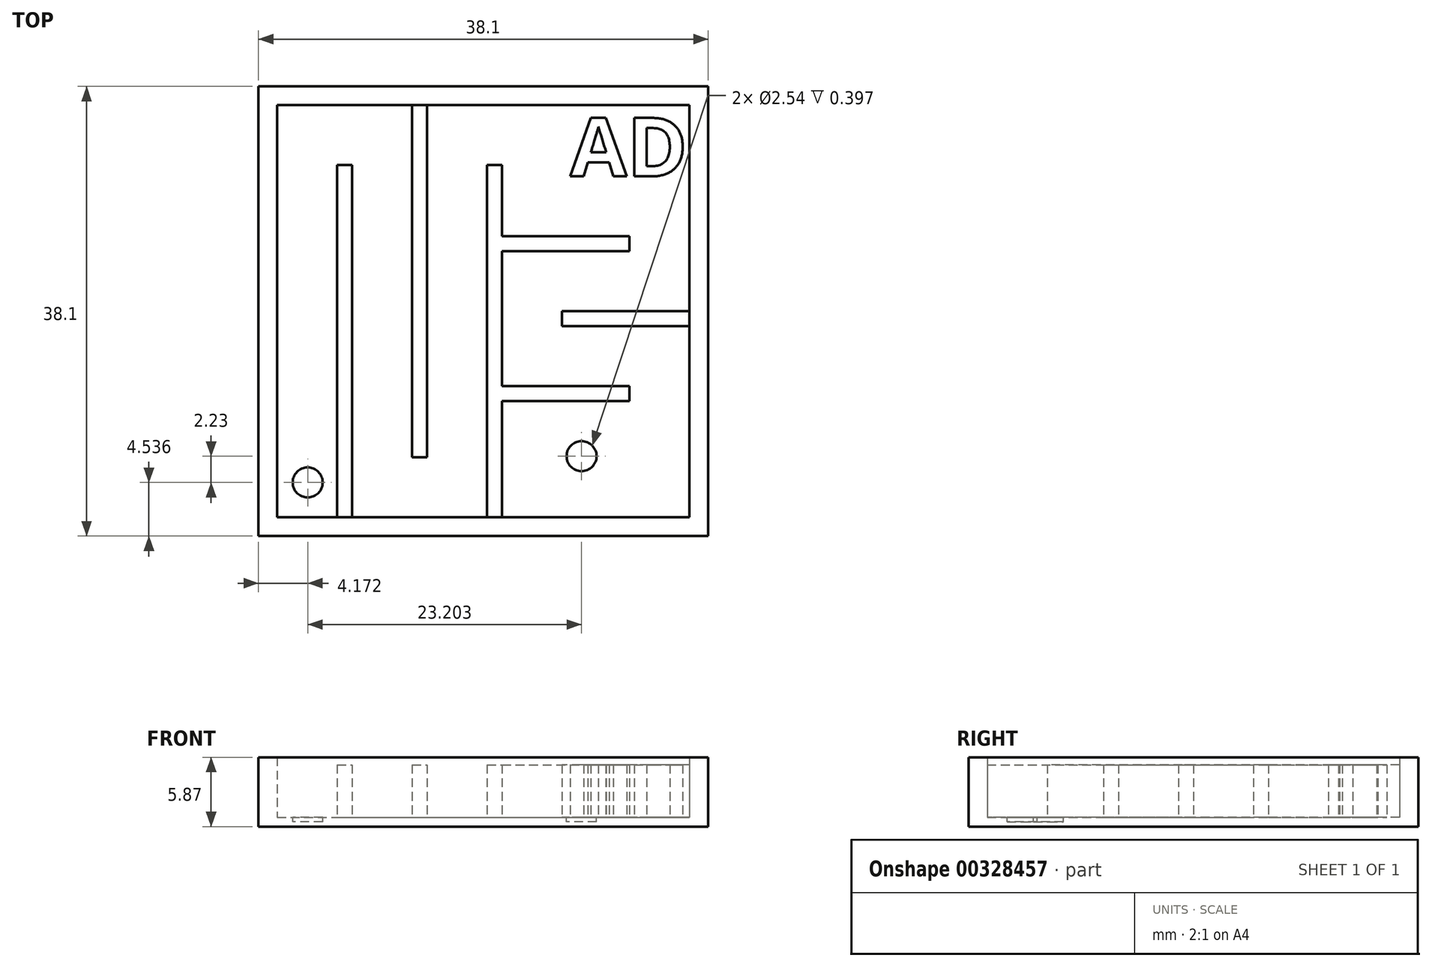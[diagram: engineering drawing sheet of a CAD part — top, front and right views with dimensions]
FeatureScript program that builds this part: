
annotation { "Feature Type Name" : "Feature", "Feature Type Description" : "" }
export const myFeature = defineFeature(function(context is Context, id is Id, definition is map)
    precondition{}
    {
        {
            var Q0;
            Q0=qCreatedBy(makeId("Top.planeOp"),FACE);
            var sketch = newSketch(context, id + "F0", { "sketchPlane" : qUnion([Q0])});
            skLineSegment(sketch, "E0.bottom", {"start": v(-18.05, 18.93) * mm, "end": v(20.05, 18.93) * mm});
            skLineSegment(sketch, "E0.top", {"start": v(-18.05, -19.17) * mm, "end": v(20.05, -19.17) * mm});
            skLineSegment(sketch, "E0.left", {"start": v(-18.05, 18.93) * mm, "end": v(-18.05, -19.17) * mm});
            skLineSegment(sketch, "E0.right", {"start": v(20.05, 18.93) * mm, "end": v(20.05, -19.17) * mm});
            skSolve(sketch);
        }
        {
            var Q0;
            Q0=makeQuery(id+"F0.imprint","IMPRINT",FACE,{"disambiguationData":[TD([[makeQuery(id+"F0.imprint","IMPRINT",EDGE,{"derivedFrom":sQuery(id+"F0.wireOp",EDGE,"E0.bottom")}),-1.0]])]});
            extrude(context, id + "F1", {"entities" : qUnion([Q0]), "depth" : 0.8 * mm});
        }
        {
            var Q0;
            Q0=makeQuery(id+"F1.opExtrude","CAP_FACE",FACE,{"disambiguationData":[OSD([sQuery(id+"F0.wireOp",EDGE,"E0.bottom"),sQuery(id+"F0.wireOp",EDGE,"E0.top"),sQuery(id+"F0.wireOp",EDGE,"E0.left"),sQuery(id+"F0.wireOp",EDGE,"E0.right")])],"isStart":false});
            var sketch = newSketch(context, id + "F2", { "sketchPlane" : qUnion([Q0])});
            skLineSegment(sketch, "E1.0", {"start": v(-16.46, 17.34) * mm, "end": v(18.46, 17.34) * mm});
            skLineSegment(sketch, "E1.1", {"start": v(-16.46, 17.34) * mm, "end": v(-16.46, -17.59) * mm});
            skLineSegment(sketch, "E1.2", {"start": v(-16.46, -17.59) * mm, "end": v(18.46, -17.59) * mm});
            skLineSegment(sketch, "E1.3", {"start": v(18.46, 17.34) * mm, "end": v(18.46, -17.59) * mm});
            skSolve(sketch);
        }
        {
            var Q0;
            Q0=makeQuery(id+"F2.imprint","IMPRINT",FACE,{"disambiguationData":[TD([[makeQuery(id+"F2.imprint","IMPRINT",EDGE,{"derivedFrom":sQuery(id+"F2.wireOp",EDGE,"E1.0")}),1.0]])]});
            extrude(context, id + "F3", {"entities" : qUnion([Q0]), "operationType" : NewBodyOperationType.ADD, "depth" : 5.08 * mm});
        }
        {
            var Q0;
            Q0=makeQuery(id+"F1.opExtrude","CAP_FACE",FACE,{"disambiguationData":[OSD([sQuery(id+"F0.wireOp",EDGE,"E0.bottom"),sQuery(id+"F0.wireOp",EDGE,"E0.top"),sQuery(id+"F0.wireOp",EDGE,"E0.left"),sQuery(id+"F0.wireOp",EDGE,"E0.right")])],"isStart":false});
            var sketch = newSketch(context, id + "F4", { "sketchPlane" : qUnion([Q0])});
            skLineSegment(sketch, "E2.bottom", {"start": v(-11.38, -17.59) * mm, "end": v(-10.11, -17.59) * mm});
            skLineSegment(sketch, "E2.top", {"start": v(-11.38, 12.26) * mm, "end": v(-10.11, 12.26) * mm});
            skLineSegment(sketch, "E2.left", {"start": v(-11.38, -17.59) * mm, "end": v(-11.38, 12.26) * mm});
            skLineSegment(sketch, "E2.right", {"start": v(-10.11, -17.59) * mm, "end": v(-10.11, 12.26) * mm});
            skLineSegment(sketch, "E3.bottom", {"start": v(-5.03, 17.34) * mm, "end": v(-3.76, 17.34) * mm});
            skLineSegment(sketch, "E3.top", {"start": v(-5.03, -12.5) * mm, "end": v(-3.76, -12.5) * mm});
            skLineSegment(sketch, "E3.left", {"start": v(-5.03, 17.34) * mm, "end": v(-5.03, -12.5) * mm});
            skLineSegment(sketch, "E3.right", {"start": v(-3.76, 17.34) * mm, "end": v(-3.76, -12.5) * mm});
            skLineSegment(sketch, "E4.bottom", {"start": v(1.32, -17.59) * mm, "end": v(2.59, -17.59) * mm});
            skLineSegment(sketch, "E4.top", {"start": v(1.32, 12.26) * mm, "end": v(2.59, 12.26) * mm});
            skLineSegment(sketch, "E4.left", {"start": v(1.32, -17.59) * mm, "end": v(1.32, 12.26) * mm});
            skLineSegment(sketch, "E4.right", {"start": v(2.59, -17.59) * mm, "end": v(2.59, 12.26) * mm});
            skLineSegment(sketch, "E5.bottom", {"start": v(2.59, 6.23) * mm, "end": v(13.38, 6.23) * mm});
            skLineSegment(sketch, "E5.top", {"start": v(2.59, 4.96) * mm, "end": v(13.38, 4.96) * mm});
            skLineSegment(sketch, "E5.left", {"start": v(2.59, 6.23) * mm, "end": v(2.59, 4.96) * mm});
            skLineSegment(sketch, "E5.right", {"start": v(13.38, 6.23) * mm, "end": v(13.38, 4.96) * mm});
            skLineSegment(sketch, "E6.bottom", {"start": v(18.46, -0.12) * mm, "end": v(7.67, -0.12) * mm});
            skLineSegment(sketch, "E6.top", {"start": v(18.46, -1.4) * mm, "end": v(7.67, -1.4) * mm});
            skLineSegment(sketch, "E6.left", {"start": v(18.46, -0.12) * mm, "end": v(18.46, -1.4) * mm});
            skLineSegment(sketch, "E6.right", {"start": v(7.67, -0.12) * mm, "end": v(7.67, -1.4) * mm});
            skLineSegment(sketch, "E7.bottom", {"start": v(2.59, -7.74) * mm, "end": v(13.38, -7.74) * mm});
            skLineSegment(sketch, "E7.top", {"start": v(2.59, -6.47) * mm, "end": v(13.38, -6.47) * mm});
            skLineSegment(sketch, "E7.left", {"start": v(2.59, -7.74) * mm, "end": v(2.59, -6.47) * mm});
            skLineSegment(sketch, "E7.right", {"start": v(13.38, -7.74) * mm, "end": v(13.38, -6.47) * mm});
            skCircle(sketch, "E8", {"center": v(9.32, -12.4) * mm, "radius": 1.27 * mm});
            skText(sketch, "E9", { "text": "AD", "fontName": "OpenSans-Bold.ttf"});
            skCircle(sketch, "E10", {"center": v(-13.88, -14.63) * mm, "radius": 1.27 * mm});
            const initialGuessF4  = {"E9": [0.00836, 0.0113, 1, 0, 0.005]};
            skSetInitialGuess(sketch, initialGuessF4);
            skSolve(sketch);
        }
        {
            var Q0;
            Q0=makeQuery(id+"F4.imprint","IMPRINT",FACE,{"disambiguationData":[TD([[makeQuery(id+"F4.imprint","IMPRINT",EDGE,{"derivedFrom":sQuery(id+"F4.wireOp",EDGE,"E2.bottom")}),1.0]])]});
            var Q1;
            Q1=makeQuery(id+"F4.imprint","IMPRINT",FACE,{"disambiguationData":[TD([[makeQuery(id+"F4.imprint","IMPRINT",EDGE,{"derivedFrom":sQuery(id+"F4.wireOp",EDGE,"E3.bottom")}),-1.0]])]});
            var Q2;
            {var subQ1=sQuery(id+"F4.wireOp",EDGE,"E4.bottom");Q2=makeQuery(id+"F4.imprint","IMPRINT",FACE,{"disambiguationData":[TD([[makeQuery(id+"F4.imprint","IMPRINT",EDGE,{"derivedFrom":subQ1}),1.0]])]});}
            var Q3;
            Q3=makeQuery(id+"F4.imprint","IMPRINT",FACE,{"disambiguationData":[TD([[makeQuery(id+"F4.imprint","IMPRINT",EDGE,{"derivedFrom":sQuery(id+"F4.wireOp",EDGE,"E7.bottom")}),1.0]])]});
            var Q4;
            Q4=makeQuery(id+"F4.imprint","IMPRINT",FACE,{"disambiguationData":[TD([[makeQuery(id+"F4.imprint","IMPRINT",EDGE,{"derivedFrom":sQuery(id+"F4.wireOp",EDGE,"E5.bottom")}),-1.0]])]});
            var Q5;
            Q5=makeQuery(id+"F4.imprint","IMPRINT",FACE,{"disambiguationData":[TD([[makeQuery(id+"F4.imprint","IMPRINT",EDGE,{"derivedFrom":sQuery(id+"F4.wireOp",EDGE,"E6.bottom")}),1.0]])]});
            extrude(context, id + "F5", {"entities" : qUnion([Q0, Q1, Q2, Q3, Q4, Q5]), "operationType" : NewBodyOperationType.ADD, "depth" : 4.44 * mm});
        }
        {
            var Q0;
            Q0=makeQuery(id+"F4.imprint","IMPRINT",FACE,{"disambiguationData":[TD([[makeQuery(id+"F4.imprint","IMPRINT",EDGE,{"derivedFrom":sQuery(id+"F4.wireOp",EDGE,"E9.sketch_text.stroke-13")}),-1.0]])]});
            var Q1;
            Q1=makeQuery(id+"F4.imprint","IMPRINT",FACE,{"disambiguationData":[TD([[makeQuery(id+"F4.imprint","IMPRINT",EDGE,{"derivedFrom":sQuery(id+"F4.wireOp",EDGE,"E9.sketch_text.stroke-0")}),-1.0]])]});
            extrude(context, id + "F6", {"entities" : qUnion([Q0, Q1]), "operationType" : NewBodyOperationType.ADD, "depth" : 4.44 * mm});
        }
        {
            var Q0;
            Q0=makeQuery(id+"F4.imprint","IMPRINT",FACE,{"disambiguationData":[TD([[makeQuery(id+"F4.imprint","IMPRINT",EDGE,{"derivedFrom":sQuery(id+"F4.wireOp",EDGE,"E8")}),1.0]])]});
            var Q1;
            Q1=makeQuery(id+"F4.imprint","IMPRINT",FACE,{"disambiguationData":[TD([[makeQuery(id+"F4.imprint","IMPRINT",EDGE,{"derivedFrom":sQuery(id+"F4.wireOp",EDGE,"E10")}),1.0]])]});
            extrude(context, id + "F7", {"entities" : qUnion([Q0, Q1]), "operationType" : NewBodyOperationType.REMOVE, "oppositeDirection" : true, "depth" : 0.4 * mm});
        }
    });
